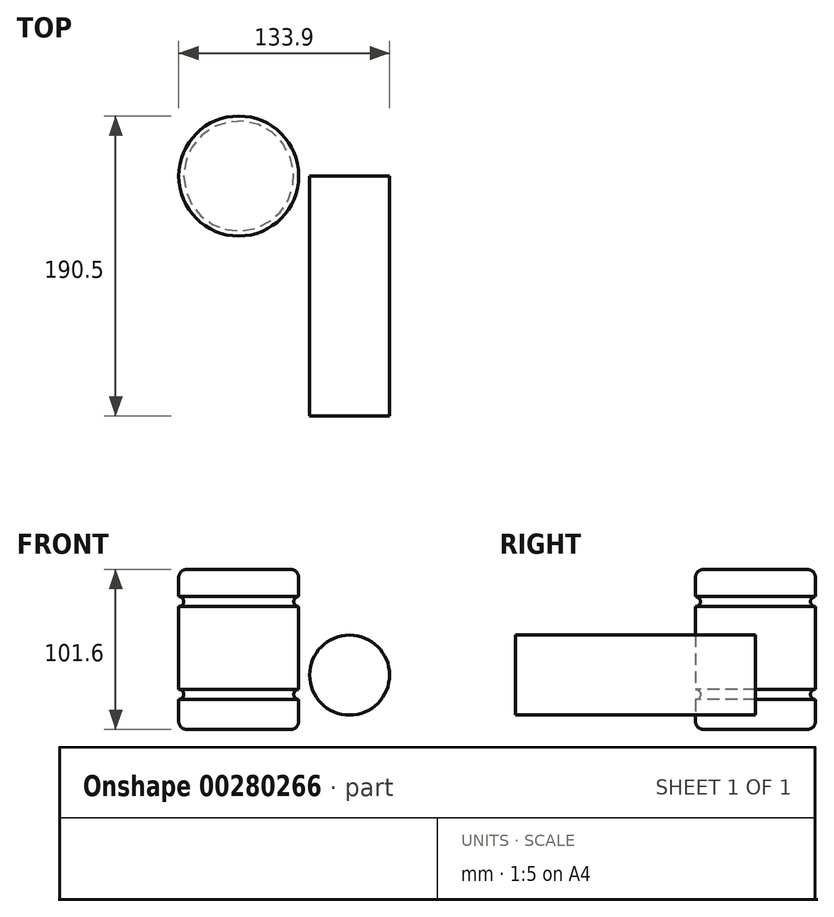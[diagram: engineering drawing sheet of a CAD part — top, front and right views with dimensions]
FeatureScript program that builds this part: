
annotation { "Feature Type Name" : "Feature", "Feature Type Description" : "" }
export const myFeature = defineFeature(function(context is Context, id is Id, definition is map)
    precondition{}
    {
        {
            var Q0;
            Q0=qCreatedBy(makeId("Front.planeOp"),FACE);
            var sketch = newSketch(context, id + "F0", { "sketchPlane" : qUnion([Q0])});
            skLineSegment(sketch, "E0.bottom", {"start": v(0, 0) * mm, "end": v(-38.1, 0) * mm});
            skLineSegment(sketch, "E0.top", {"start": v(0, 101.6) * mm, "end": v(-38.1, 101.6) * mm});
            skLineSegment(sketch, "E0.left", {"start": v(0, 0) * mm, "end": v(0, 101.6) * mm});
            skLineSegment(sketch, "E0.right", {"start": v(-38.1, 0) * mm, "end": v(-38.1, 101.6) * mm});
            skCircle(sketch, "E1", {"center": v(0, 81.21) * mm, "radius": 3.18 * mm});
            skCircle(sketch, "E2", {"center": v(0, 22.27) * mm, "radius": 3.18 * mm});
            skSolve(sketch);
        }
        {
            var Q0;
            {var subQ5=sQuery(id+"F0.wireOp",EDGE,"E0.bottom");Q0=makeQuery(id+"F0.imprint","IMPRINT",FACE,{"disambiguationData":[TD([[makeQuery(id+"F0.imprint","IMPRINT",EDGE,{"derivedFrom":subQ5}),-1.0]])]});}
            var Q1;
            Q1=sQuery(id+"F0.wireOp",EDGE,"E0.right");
            revolve(context, id + "F1", {"entities" : qUnion([Q0]), "axis" : qUnion([Q1]), "revolveType" : RevolveType.FULL});
        }
        {
            var Q0;
            Q0=makeQuery(id+"F1.opRevolve","SWEPT_FACE",FACE,{"disambiguationData":[OSD([sQuery(id+"F0.wireOp",EDGE,"E0.top")])]});
            var Q1;
            Q1=makeQuery(id+"F1.opRevolve","SWEPT_FACE",FACE,{"disambiguationData":[OSD([sQuery(id+"F0.wireOp",EDGE,"E0.bottom")])]});
            fillet(context, id + "F2", {"entities" : qUnion([Q0, Q1]), "radius" : 5.08 * mm, "tangentPropagation" : true, "allowEdgeOverflow" : false});
        }
        {
            var Q0;
            Q0=qCreatedBy(makeId("Front.planeOp"),FACE);
            var sketch = newSketch(context, id + "F3", { "sketchPlane" : qUnion([Q0])});
            skCircle(sketch, "E3", {"center": v(32.3, 34.53) * mm, "radius": 25.4 * mm});
            skSolve(sketch);
        }
        {
            var Q0;
            Q0 = qSketchRegion(id + "F3", true);
            extrude(context, id + "F4", {"entities" : qUnion([Q0]), "depth" : 152.4 * mm});
        }
    });
